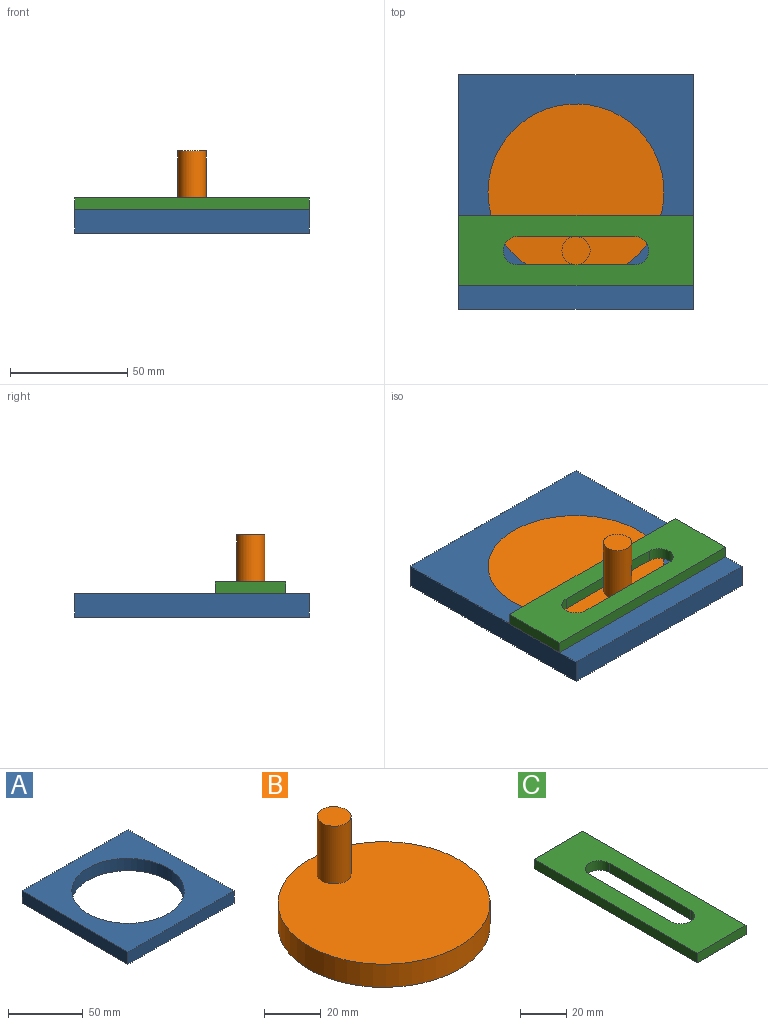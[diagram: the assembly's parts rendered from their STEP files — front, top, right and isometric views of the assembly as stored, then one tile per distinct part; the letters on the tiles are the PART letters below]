
ASSEMBLY  parts=3 mates=3
PART A: 7 faces, bbox 100x100x10 mm
  f0: plane 100x10mm, normal (0,-1,0), area 1000mm2, adj f1,f4,f5,f6
  f1: plane 100x10mm, normal (-1,0,0), area 1000mm2, adj f0,f2,f5,f6
  f2: plane 100x10mm, normal (0,1,0), area 1000mm2, adj f1,f4,f5,f6
  f3: cylinder r=37.5mm len=75mm, axis (0,0,-1), area 2356.2mm2, adj f5,f6
  f4: plane 100x10mm, normal (1,0,0), area 1000mm2, adj f0,f2,f5,f6
  f5: plane 100x100mm, normal (0,0,1), area 5582.1mm2, adj f0,f1,f2,f3,f4
  f6: plane 100x100mm, normal (0,0,-1), area 5582.1mm2, adj f0,f1,f2,f3,f4
PART B: 5 faces, bbox 75x75x35 mm
  f0: cylinder r=37.5mm len=75mm, axis (0,0,-1), area 2356.2mm2, adj f1,f2
  f1: plane 75x75mm, normal (0,0,1), area 4304.8mm2, adj f0,f3
  f2: plane 75x75mm, normal (0,0,-1), area 4417.9mm2, adj f0
  f3: cylinder r=6mm len=25mm, axis (0,0,-1), area 942.5mm2, adj f1,f4
  f4: plane 12x12mm, normal (0,0,1), area 113.1mm2, adj f3
PART C: 10 faces, bbox 30x100x5 mm
  f0: plane 50x5mm, normal (1,0,0), area 250mm2, adj f1,f7,f8,f9
  f1: cylinder r=6mm len=12mm, axis (0,0,-1), area 94.2mm2, adj f0,f2,f8,f9
  f2: plane 50x5mm, normal (-1,0,0), area 250mm2, adj f1,f7,f8,f9
  f3: plane 30x5mm, normal (0,1,0), area 150mm2, adj f4,f6,f8,f9
  f4: plane 100x5mm, normal (-1,0,0), area 500mm2, adj f3,f5,f8,f9
  f5: plane 30x5mm, normal (0,-1,0), area 150mm2, adj f4,f6,f8,f9
  f6: plane 100x5mm, normal (1,0,0), area 500mm2, adj f3,f5,f8,f9
  f7: cylinder r=6mm len=12mm, axis (0,0,-1), area 94.2mm2, adj f0,f2,f8,f9
  f8: plane 100x30mm, normal (0,0,1), area 2286.9mm2, adj f0,f1,f2,f3,f4,f5,f6,f7
  f9: plane 100x30mm, normal (0,0,-1), area 2286.9mm2, adj f0,f1,f2,f3,f4,f5,f6,f7
PLACE A rot(axis=(0,0,1),180deg) t=(0,0,0)mm
PLACE B rot(axis=(0,0,1),180deg) t=(0,0,0)mm
PLACE C rot(axis=(0.71,-0.71,0),180deg) t=(0,-25,25)mm
MATE planar C.f8 <-> A.f5  axis (0,0,-1) through (50,-25,10)mm
MATE planar C.f3 <-> A.f4  axis (-1,0,0) through (-50,-25,15)mm
MATE pin_slot B.f3 <-> C.f1  axis (0,0,1) through (0,-25,35)mm
